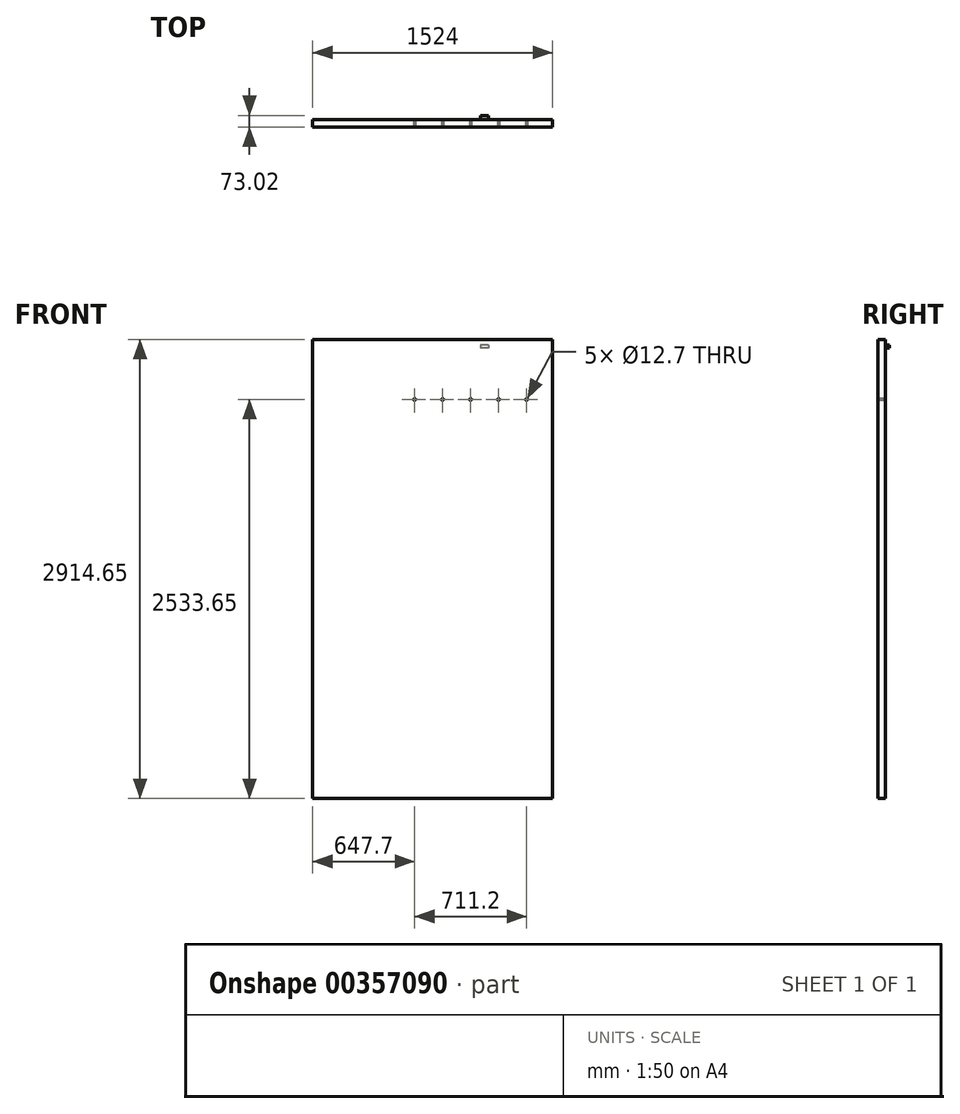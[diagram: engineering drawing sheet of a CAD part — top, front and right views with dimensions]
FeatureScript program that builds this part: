
annotation { "Feature Type Name" : "Feature", "Feature Type Description" : "" }
export const myFeature = defineFeature(function(context is Context, id is Id, definition is map)
    precondition{}
    {
        {
            var Q0;
            Q0=qCreatedBy(makeId("Top.planeOp"),FACE);
            var sketch = newSketch(context, id + "F0", { "sketchPlane" : qUnion([Q0])});
            skLineSegment(sketch, "E0.bottom", {"start": v(762, -23.81) * mm, "end": v(-762, -23.81) * mm});
            skLineSegment(sketch, "E0.top", {"start": v(762, 23.81) * mm, "end": v(-762, 23.81) * mm});
            skLineSegment(sketch, "E0.left", {"start": v(762, -23.81) * mm, "end": v(762, 23.81) * mm});
            skLineSegment(sketch, "E0.right", {"start": v(-762, -23.81) * mm, "end": v(-762, 23.81) * mm});
            skPoint(sketch, "E0.middle", {"position": v(0, 0) * mm});
            skSolve(sketch);
        }
        {
            var Q0;
            Q0=makeQuery(id+"F0.imprint","IMPRINT",FACE,{"disambiguationData":[TD([[makeQuery(id+"F0.imprint","IMPRINT",EDGE,{"derivedFrom":sQuery(id+"F0.wireOp",EDGE,"E0.bottom")}),-1.0]])]});
            extrude(context, id + "F1", {"entities" : qUnion([Q0]), "depth" : 2914.65 * mm});
        }
        {
            var Q0;
            Q0=makeQuery(id+"F1.opExtrude","SWEPT_FACE",FACE,{"disambiguationData":[OSD([sQuery(id+"F0.wireOp",EDGE,"E0.bottom")])]});
            var sketch = newSketch(context, id + "F2", { "sketchPlane" : qUnion([Q0])});
            skPoint(sketch, "E1", {"position": v(-762, 1457.33) * mm});
            skPoint(sketch, "E2.0.2.0", {"position": v(1081.7, 5701.03) * mm});
            skPoint(sketch, "E2.0.3.0", {"position": v(1081.7, 8487.41) * mm});
            skPoint(sketch, "E2.0.4.0", {"position": v(1081.7, 11273.8) * mm});
            skPoint(sketch, "E2.0.5.0", {"position": v(1081.7, 14060.17) * mm});
            skPoint(sketch, "E2.0.6.0", {"position": v(1081.7, 16846.55) * mm});
            skPoint(sketch, "E2.1.2.0", {"position": v(1107.1, 5701.03) * mm});
            skPoint(sketch, "E2.1.3.0", {"position": v(1107.1, 8487.41) * mm});
            skPoint(sketch, "E2.1.4.0", {"position": v(1107.1, 11273.8) * mm});
            skPoint(sketch, "E2.1.5.0", {"position": v(1107.1, 14060.17) * mm});
            skPoint(sketch, "E2.1.6.0", {"position": v(1107.1, 16846.55) * mm});
            skPoint(sketch, "E2.2.2.0", {"position": v(1132.5, 5701.03) * mm});
            skPoint(sketch, "E2.2.3.0", {"position": v(1132.5, 8487.41) * mm});
            skPoint(sketch, "E2.2.4.0", {"position": v(1132.5, 11273.8) * mm});
            skPoint(sketch, "E2.2.5.0", {"position": v(1132.5, 14060.17) * mm});
            skPoint(sketch, "E2.2.6.0", {"position": v(1132.5, 16846.55) * mm});
            skLineSegment(sketch, "E3", {"start": v(1704.2, 2533.65) * mm, "end": v(-1266.13, 2533.65) * mm, "construction": true});
            skLineSegment(sketch, "E4", {"start": v(1805.63, 2025.65) * mm, "end": v(-1549.3, 2025.65) * mm, "construction": true});
            skLineSegment(sketch, "E5", {"start": v(1764.18, 1517.65) * mm, "end": v(-1241.62, 1517.65) * mm, "construction": true});
            skLineSegment(sketch, "E6", {"start": v(1830.9, 1009.65) * mm, "end": v(-1410.2, 1009.65) * mm, "construction": true});
            skLineSegment(sketch, "E7", {"start": v(1838.9, 501.65) * mm, "end": v(-1203.85, 501.65) * mm, "construction": true});
            skPoint(sketch, "E8", {"position": v(596.9, 2533.65) * mm});
            skPoint(sketch, "E9", {"position": v(419.1, 2533.65) * mm});
            skPoint(sketch, "E10", {"position": v(241.3, 2533.65) * mm});
            skPoint(sketch, "E11", {"position": v(63.5, 2533.65) * mm});
            skPoint(sketch, "E12", {"position": v(-114.3, 2533.65) * mm});
            skCircle(sketch, "E13", {"center": v(-114.3, 2533.65) * mm, "radius": 6.35 * mm});
            skCircle(sketch, "E14.1.0.0", {"center": v(63.5, 2533.65) * mm, "radius": 6.35 * mm});
            skCircle(sketch, "E14.2.0.0", {"center": v(241.3, 2533.65) * mm, "radius": 6.35 * mm});
            skCircle(sketch, "E14.3.0.0", {"center": v(419.1, 2533.65) * mm, "radius": 6.35 * mm});
            skCircle(sketch, "E14.4.0.0", {"center": v(596.9, 2533.65) * mm, "radius": 6.35 * mm});
            skLineSegment(sketch, "E14.direction1", {"start": v(-114.3, 2533.65) * mm, "end": v(63.5, 2533.65) * mm, "construction": true});
            skSolve(sketch);
        }
        {
            var Q0;
            Q0=makeQuery(id+"F2.imprint","IMPRINT",FACE,{"disambiguationData":[TD([[makeQuery(id+"F2.imprint","IMPRINT",EDGE,{"derivedFrom":sQuery(id+"F2.wireOp",EDGE,"E13")}),1.0]])]});
            var Q1;
            Q1=makeQuery(id+"F2.imprint","IMPRINT",FACE,{"disambiguationData":[TD([[makeQuery(id+"F2.imprint","IMPRINT",EDGE,{"derivedFrom":sQuery(id+"F2.wireOp",EDGE,"E14.1.0.0")}),1.0]])]});
            var Q2;
            Q2=makeQuery(id+"F2.imprint","IMPRINT",FACE,{"disambiguationData":[TD([[makeQuery(id+"F2.imprint","IMPRINT",EDGE,{"derivedFrom":sQuery(id+"F2.wireOp",EDGE,"E14.2.0.0")}),1.0]])]});
            var Q3;
            Q3=makeQuery(id+"F2.imprint","IMPRINT",FACE,{"disambiguationData":[TD([[makeQuery(id+"F2.imprint","IMPRINT",EDGE,{"derivedFrom":sQuery(id+"F2.wireOp",EDGE,"E14.3.0.0")}),1.0]])]});
            var Q4;
            Q4=makeQuery(id+"F2.imprint","IMPRINT",FACE,{"disambiguationData":[TD([[makeQuery(id+"F2.imprint","IMPRINT",EDGE,{"derivedFrom":sQuery(id+"F2.wireOp",EDGE,"E14.4.0.0")}),1.0]])]});
            var Q5;
            Q5=makeQuery(id+"F1.opExtrude","SWEPT_FACE",FACE,{"disambiguationData":[OSD([sQuery(id+"F0.wireOp",EDGE,"E0.top")])]});
            extrude(context, id + "F3", {"entities" : qUnion([Q0, Q1, Q2, Q3, Q4]), "operationType" : NewBodyOperationType.REMOVE, "endBound" : BoundingType.THROUGH_ALL, "oppositeDirection" : true, "endBoundEntityFace" : qUnion([Q5]), "depth" : 25.4 * mm});
        }
        {
            var Q0;
            Q0=makeQuery(id+"F1.opExtrude","SWEPT_FACE",FACE,{"disambiguationData":[OSD([sQuery(id+"F0.wireOp",EDGE,"E0.top")])]});
            var sketch = newSketch(context, id + "F4", { "sketchPlane" : qUnion([Q0])});
            skLineSegment(sketch, "E15.bottom", {"start": v(-355.6, 2879.1) * mm, "end": v(-304.8, 2879.1) * mm});
            skLineSegment(sketch, "E15.top", {"start": v(-355.6, 2860.04) * mm, "end": v(-304.8, 2860.04) * mm});
            skLineSegment(sketch, "E15.left", {"start": v(-355.6, 2879.1) * mm, "end": v(-355.6, 2860.04) * mm});
            skLineSegment(sketch, "E15.right", {"start": v(-304.8, 2879.1) * mm, "end": v(-304.8, 2860.04) * mm});
            skSolve(sketch);
        }
        {
            var Q0;
            Q0=makeQuery(id+"F4.imprint","IMPRINT",FACE,{"disambiguationData":[TD([[makeQuery(id+"F4.imprint","IMPRINT",EDGE,{"derivedFrom":sQuery(id+"F4.wireOp",EDGE,"E15.bottom")}),-1.0]])]});
            extrude(context, id + "F5", {"entities" : qUnion([Q0]), "operationType" : NewBodyOperationType.ADD, "depth" : 25.4 * mm});
        }
    });
